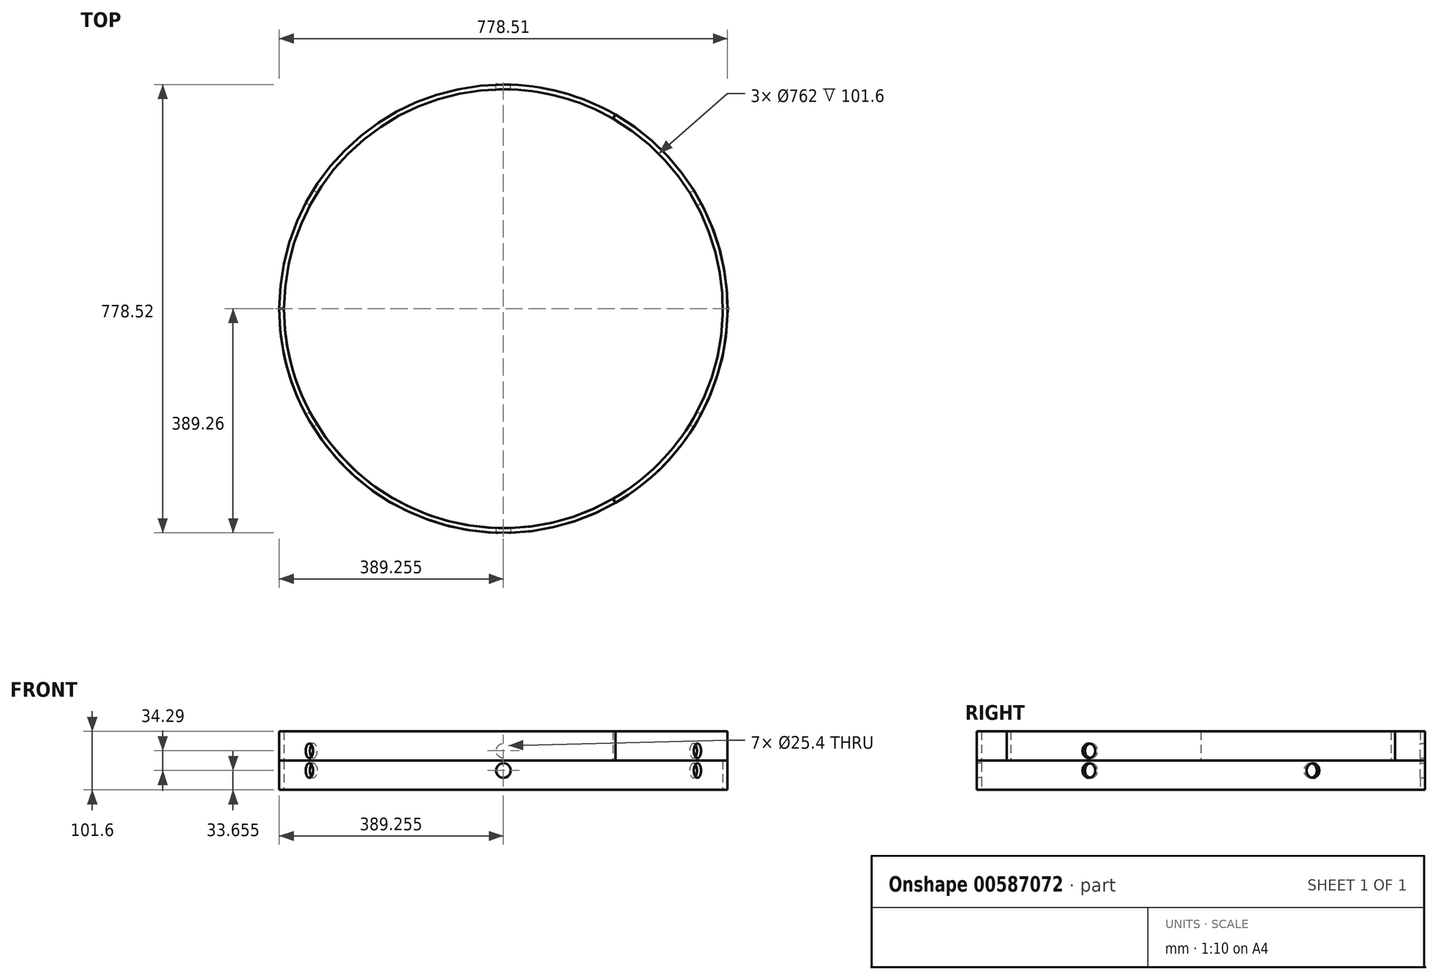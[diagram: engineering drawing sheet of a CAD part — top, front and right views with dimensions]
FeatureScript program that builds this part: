
annotation { "Feature Type Name" : "Feature", "Feature Type Description" : "" }
export const myFeature = defineFeature(function(context is Context, id is Id, definition is map)
    precondition{}
    {
        {
            var Q0;
            Q0=qCreatedBy(makeId("Front.planeOp"),FACE);
            var sketch = newSketch(context, id + "F0", { "sketchPlane" : qUnion([Q0])});
            skLineSegment(sketch, "E0.bottom", {"start": v(0, 50.8) * mm, "end": v(8.26, 50.8) * mm});
            skLineSegment(sketch, "E0.top", {"start": v(0, 0) * mm, "end": v(8.26, 0) * mm});
            skLineSegment(sketch, "E0.left", {"start": v(0, 50.8) * mm, "end": v(0, 0) * mm});
            skLineSegment(sketch, "E0.right", {"start": v(8.26, 50.8) * mm, "end": v(8.26, 0) * mm});
            skLineSegment(sketch, "E1", {"start": v(0, 0) * mm, "end": v(389.26, 0) * mm});
            skLineSegment(sketch, "E2", {"start": v(389.26, -92.79) * mm, "end": v(389.26, 0) * mm, "construction": true});
            skSolve(sketch);
        }
        {
            var Q0;
            Q0=makeQuery(id+"F0.imprint","IMPRINT",FACE,{"disambiguationData":[TD([[makeQuery(id+"F0.imprint","IMPRINT",EDGE,{"derivedFrom":sQuery(id+"F0.wireOp",EDGE,"E0.bottom")}),-1.0]])]});
            var Q1;
            Q1=sQuery(id+"F0.wireOp",EDGE,"E2");
            revolve(context, id + "F1", {"entities" : qUnion([Q0]), "axis" : qUnion([Q1]), "revolveType" : RevolveType.TWO_DIRECTIONS, "angle" : 30 * degree, "angleBack" : 330 * degree});
        }
        {
            var Q0;
            Q0=qCreatedBy(makeId("Right.planeOp"),FACE);
            var sketch = newSketch(context, id + "F2", { "sketchPlane" : qUnion([Q0])});
            skPoint(sketch, "E3", {"position": v(0, 33.66) * mm});
            skCircle(sketch, "E4", {"center": v(0, 33.66) * mm, "radius": 12.7 * mm});
            skSolve(sketch);
        }
        {
            var Q0;
            Q0=sQuery(id+"F2.wireOp",VERTEX,"E3");
            var Q1;
            Q1=makeQuery(id+"F1.opRevolve","SWEPT_BODY",BODY,{"disambiguationData":[OSD([sQuery(id+"F0.wireOp",EDGE,"E0.bottom"),sQuery(id+"F0.wireOp",EDGE,"E0.left"),sQuery(id+"F0.wireOp",EDGE,"E0.right"),sQuery(id+"F0.wireOp",EDGE,"E1")])]});
            hole(context, id + "F3", {"style" : HoleStyle.SIMPLE, "endStyle" : HoleEndStyle.THROUGH, "oppositeDirection" : true, "holeDiameter" : 25.4 * mm, "majorDiameter" : 6.35 * mm, "isTappedThrough" : true, "tappedDepth" : 12.7 * mm, "tapClearance" : 3, "locations" : qUnion([Q0]), "scope" : qUnion([Q1])});
        }
        {
            var Q0;
            Q0=qCreatedBy(makeId("Front.planeOp"),FACE);
            var sketch = newSketch(context, id + "F4", { "sketchPlane" : qUnion([Q0])});
            skLineSegment(sketch, "E5.bottom", {"start": v(0, 101.6) * mm, "end": v(8.26, 101.6) * mm});
            skLineSegment(sketch, "E5.top", {"start": v(0, 50.8) * mm, "end": v(8.26, 50.8) * mm});
            skLineSegment(sketch, "E5.left", {"start": v(0, 101.6) * mm, "end": v(0, 50.8) * mm});
            skLineSegment(sketch, "E5.right", {"start": v(8.25, 101.6) * mm, "end": v(8.25, 50.8) * mm});
            skLineSegment(sketch, "E6", {"start": v(0, 50.8) * mm, "end": v(389.26, 50.8) * mm});
            skLineSegment(sketch, "E7", {"start": v(389.26, -101.99) * mm, "end": v(389.26, 50.8) * mm, "construction": true});
            skSolve(sketch);
        }
        {
            var Q0;
            Q0 = qSketchRegion(id + "F4", true);
            var Q1;
            Q1=sQuery(id+"F4.wireOp",EDGE,"E7");
            revolve(context, id + "F5", {"entities" : qUnion([Q0]), "axis" : qUnion([Q1]), "revolveType" : RevolveType.TWO_DIRECTIONS, "angle" : 90 * degree, "angleBack" : 330 * degree});
        }
        {
            var Q0;
            Q0=qCreatedBy(makeId("Right.planeOp"),FACE);
            var sketch = newSketch(context, id + "F6", { "sketchPlane" : qUnion([Q0])});
            skPoint(sketch, "E8", {"position": v(0, 67.94) * mm});
            skSolve(sketch);
        }
        {
            var Q0;
            Q0=sQuery(id+"F6.wireOp",VERTEX,"E8");
            var Q1;
            Q1=makeQuery(id+"F5.opRevolve","SWEPT_BODY",BODY,{"disambiguationData":[OSD([sQuery(id+"F4.wireOp",EDGE,"E5.bottom"),sQuery(id+"F4.wireOp",EDGE,"E5.left"),sQuery(id+"F4.wireOp",EDGE,"E5.right"),sQuery(id+"F4.wireOp",EDGE,"E6")])]});
            hole(context, id + "F7", {"style" : HoleStyle.SIMPLE, "endStyle" : HoleEndStyle.THROUGH, "oppositeDirection" : true, "holeDiameter" : 25.4 * mm, "majorDiameter" : 6.35 * mm, "isTappedThrough" : true, "tappedDepth" : 12.7 * mm, "tapClearance" : 3, "locations" : qUnion([Q0]), "scope" : qUnion([Q1])});
        }
        {
            var Q0;
            Q0=makeQuery(id+"F1.opRevolve","SWEPT_BODY",BODY,{"disambiguationData":[OSD([sQuery(id+"F0.wireOp",EDGE,"E0.bottom"),sQuery(id+"F0.wireOp",EDGE,"E0.left"),sQuery(id+"F0.wireOp",EDGE,"E0.right"),sQuery(id+"F0.wireOp",EDGE,"E1")])]});
            var Q1;
            Q1=sQuery(id+"F4.wireOp",EDGE,"E7");
            circularPattern(context, id + "F8", {"operationType" : NewBodyOperationType.ADD, "entities" : qUnion([Q0]), "axis" : qUnion([Q1]), "angle" : 360 * degree, "instanceCount" : 6, "equalSpace" : true});
        }
        {
            var Q0;
            Q0=makeQuery(id+"F5.opRevolve","SWEPT_BODY",BODY,{"disambiguationData":[OSD([sQuery(id+"F4.wireOp",EDGE,"E5.bottom"),sQuery(id+"F4.wireOp",EDGE,"E5.left"),sQuery(id+"F4.wireOp",EDGE,"E5.right"),sQuery(id+"F4.wireOp",EDGE,"E6")])]});
            var Q1;
            Q1=sQuery(id+"F4.wireOp",EDGE,"E7");
            circularPattern(context, id + "F9", {"entities" : qUnion([Q0]), "axis" : qUnion([Q1]), "angle" : 360 * degree, "instanceCount" : 3, "equalSpace" : true});
        }
        {
            var Q0;
            Q0=makeQuery(id+"F9.opPattern","COPY",BODY,{"derivedFrom":makeQuery(id+"F5.opRevolve","SWEPT_BODY",BODY,{"disambiguationData":[OSD([sQuery(id+"F4.wireOp",EDGE,"E5.bottom"),sQuery(id+"F4.wireOp",EDGE,"E5.left"),sQuery(id+"F4.wireOp",EDGE,"E5.right"),sQuery(id+"F4.wireOp",EDGE,"E6")])]}),"instanceName":"1"});
            var Q1;
            Q1=makeQuery(id+"F9.opPattern","COPY",BODY,{"derivedFrom":makeQuery(id+"F5.opRevolve","SWEPT_BODY",BODY,{"disambiguationData":[OSD([sQuery(id+"F4.wireOp",EDGE,"E5.bottom"),sQuery(id+"F4.wireOp",EDGE,"E5.left"),sQuery(id+"F4.wireOp",EDGE,"E5.right"),sQuery(id+"F4.wireOp",EDGE,"E6")])]}),"instanceName":"2"});
            var Q2;
            Q2=makeQuery(id+"F5.opRevolve","SWEPT_BODY",BODY,{"disambiguationData":[OSD([sQuery(id+"F4.wireOp",EDGE,"E5.bottom"),sQuery(id+"F4.wireOp",EDGE,"E5.left"),sQuery(id+"F4.wireOp",EDGE,"E5.right"),sQuery(id+"F4.wireOp",EDGE,"E6")])]});
            var Q3;
            Q3=sQuery(id+"F4.wireOp",EDGE,"E7");
            var Q4;
            Q4=sQuery(id+"F4.wireOp",EDGE,"E7");
            transform(context, id + "F10", {"entities" : qUnion([Q0, Q1, Q2]), "transformType" : TransformType.ROTATION, "transformAxis" : qUnion([Q4]), "angle" : 30 * degree, "makeCopy" : false});
        }
    });
